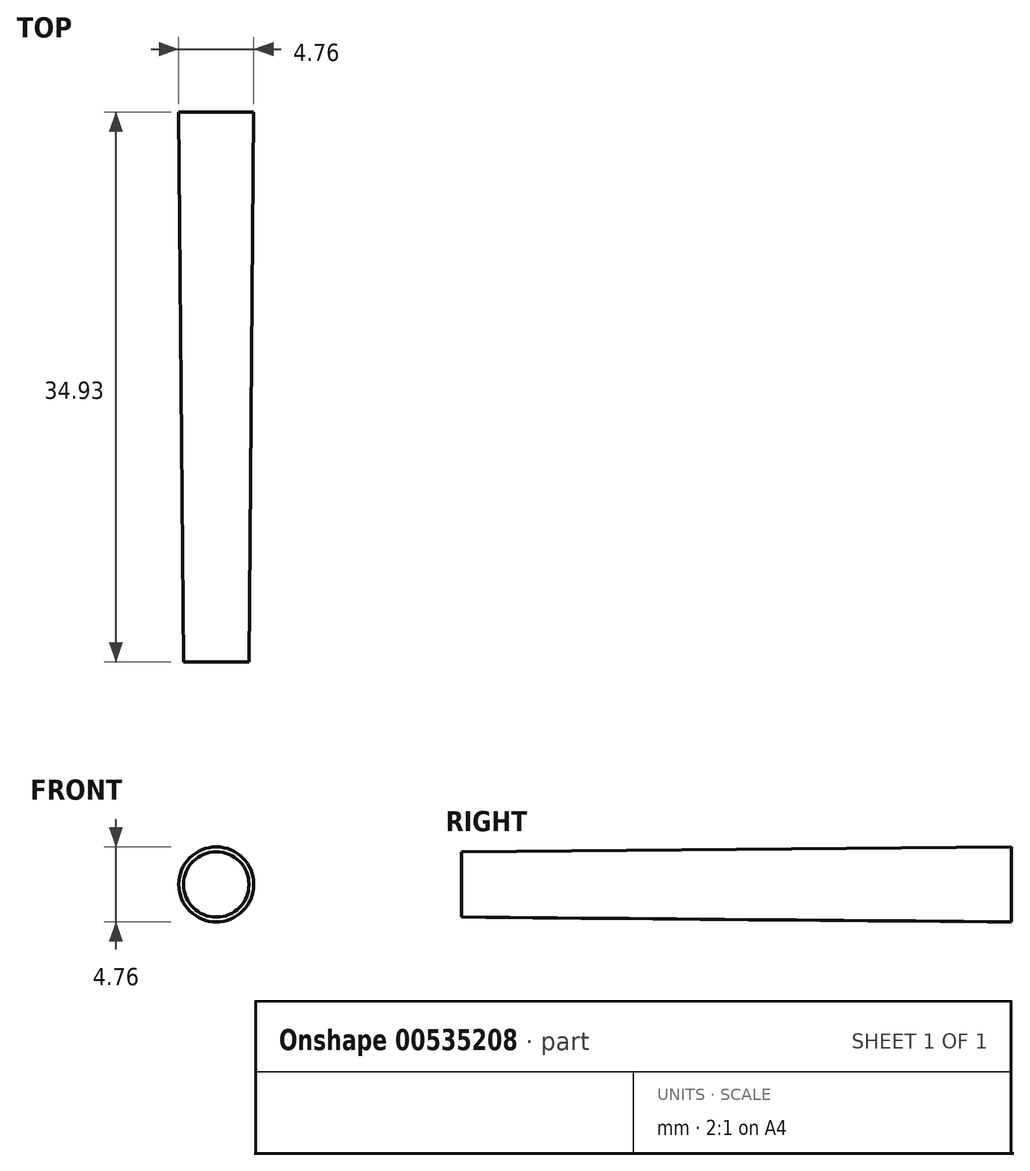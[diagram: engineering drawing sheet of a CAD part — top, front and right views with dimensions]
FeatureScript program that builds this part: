
annotation { "Feature Type Name" : "Feature", "Feature Type Description" : "" }
export const myFeature = defineFeature(function(context is Context, id is Id, definition is map)
    precondition{}
    {
        {
            var Q0;
            Q0=qCreatedBy(makeId("Front.planeOp"),FACE);
            var sketch = newSketch(context, id + "F0", { "sketchPlane" : qUnion([Q0])});
            skCircle(sketch, "E0", {"center": v(0, 0) * mm, "radius": 2.38 * mm});
            skSolve(sketch);
        }
        {
            var Q0;
            Q0=makeQuery(id+"F0.imprint","IMPRINT",FACE,{"disambiguationData":[TD([[makeQuery(id+"F0.imprint","IMPRINT",EDGE,{"derivedFrom":sQuery(id+"F0.wireOp",EDGE,"E0")}),1.0]])]});
            extrude(context, id + "F1", {"entities" : qUnion([Q0]), "depth" : 34.92 * mm, "offsetDistance" : 25.4 * mm, "hasDraft" : true, "draftAngle" : .5 * degree, "draftPullDirection" : true});
        }
    });
